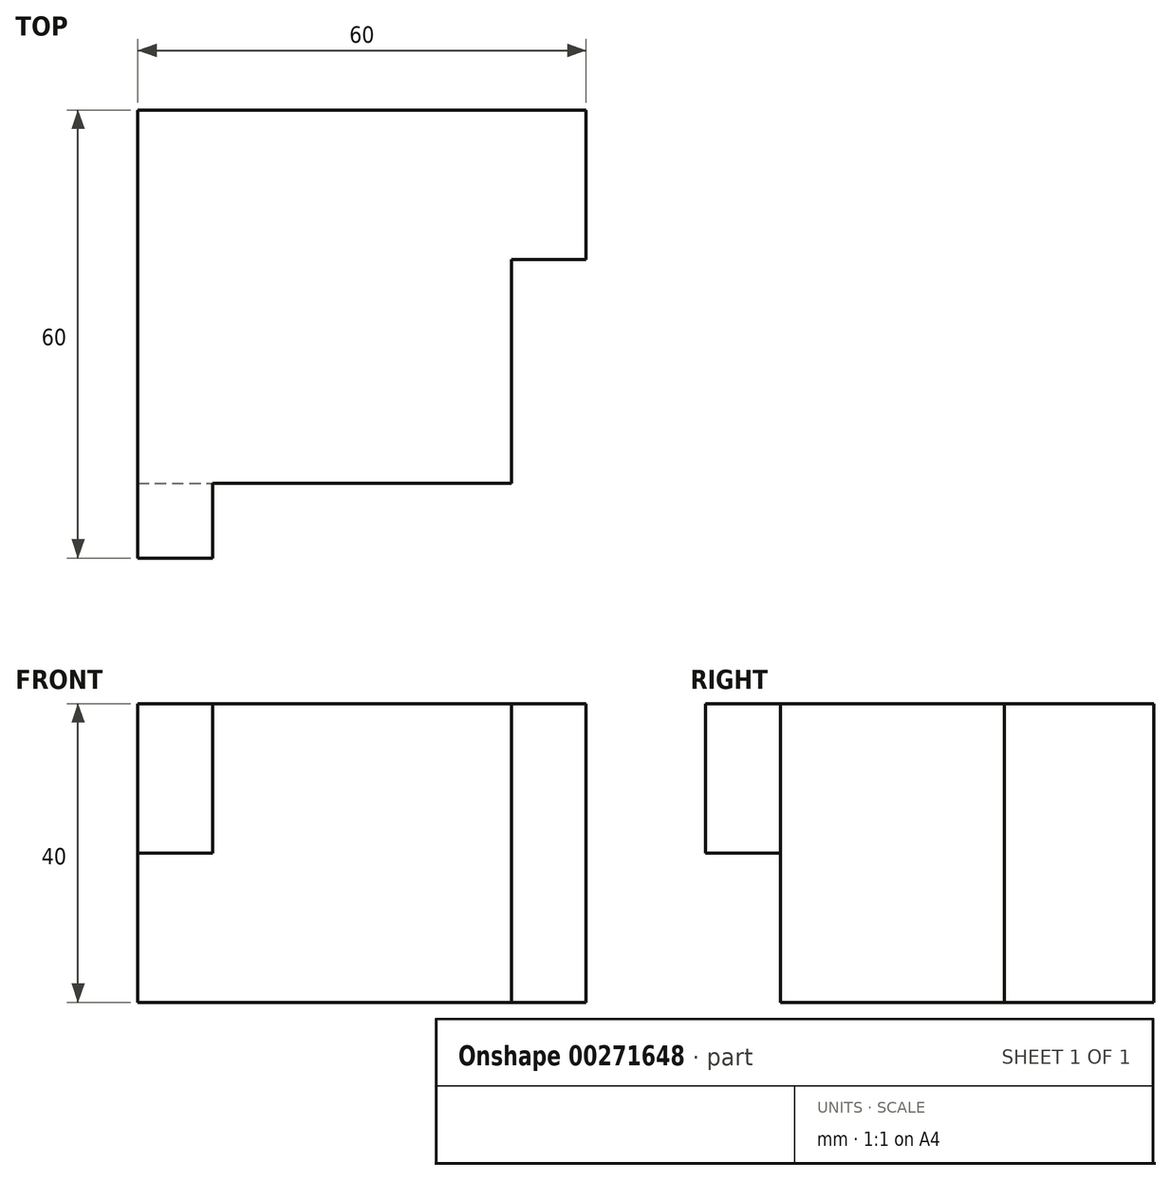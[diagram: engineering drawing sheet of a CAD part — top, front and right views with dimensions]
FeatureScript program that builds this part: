
annotation { "Feature Type Name" : "Feature", "Feature Type Description" : "" }
export const myFeature = defineFeature(function(context is Context, id is Id, definition is map)
    precondition{}
    {
        {
            var Q0;
            Q0=qCreatedBy(makeId("Top.planeOp"),FACE);
            var sketch = newSketch(context, id + "F0", { "sketchPlane" : qUnion([Q0])});
            skLineSegment(sketch, "E0.top", {"start": v(30, 30) * mm, "end": v(-30, 30) * mm});
            skLineSegment(sketch, "E0.left", {"start": v(30, 10) * mm, "end": v(30, 30) * mm});
            skLineSegment(sketch, "E0.right", {"start": v(-30, -20) * mm, "end": v(-30, 30) * mm});
            skPoint(sketch, "E0.middle", {"position": v(0, 0) * mm});
            skLineSegment(sketch, "E1.0", {"start": v(20, -20) * mm, "end": v(-30, -20) * mm});
            skLineSegment(sketch, "E2.0", {"start": v(20, -20) * mm, "end": v(20, 10) * mm});
            skPoint(sketch, "E3.orphan", {"position": v(30, -30) * mm});
            skPoint(sketch, "E4.orphan", {"position": v(-30, -30) * mm});
            skLineSegment(sketch, "E5.0", {"start": v(30, 10) * mm, "end": v(20, 10) * mm});
            skSolve(sketch);
        }
        {
            var Q0;
            Q0=makeQuery(id+"F0.imprint","IMPRINT",FACE,{"disambiguationData":[TD([[makeQuery(id+"F0.imprint","IMPRINT",EDGE,{"derivedFrom":sQuery(id+"F0.wireOp",EDGE,"E0.top")}),1.0]])]});
            extrude(context, id + "F1", {"entities" : qUnion([Q0]), "depth" : 40 * mm});
        }
        {
            var Q0;
            Q0=makeQuery(id+"F1.opExtrude","SWEPT_FACE",FACE,{"disambiguationData":[OSD([sQuery(id+"F0.wireOp",EDGE,"E1.0")])]});
            var sketch = newSketch(context, id + "F2", { "sketchPlane" : qUnion([Q0])});
            skLineSegment(sketch, "E6.bottom", {"start": v(-30, 40) * mm, "end": v(-20, 40) * mm});
            skLineSegment(sketch, "E6.top", {"start": v(-30, 20) * mm, "end": v(-20, 20) * mm});
            skLineSegment(sketch, "E6.left", {"start": v(-30, 40) * mm, "end": v(-30, 20) * mm});
            skLineSegment(sketch, "E6.right", {"start": v(-20, 40) * mm, "end": v(-20, 20) * mm});
            skSolve(sketch);
        }
        {
            var Q0;
            Q0=makeQuery(id+"F2.imprint","IMPRINT",FACE,{"disambiguationData":[TD([[makeQuery(id+"F2.imprint","IMPRINT",EDGE,{"derivedFrom":sQuery(id+"F2.wireOp",EDGE,"E6.bottom")}),1.0]])]});
            extrude(context, id + "F3", {"entities" : qUnion([Q0]), "operationType" : NewBodyOperationType.ADD, "depth" : 10 * mm});
        }
    });
